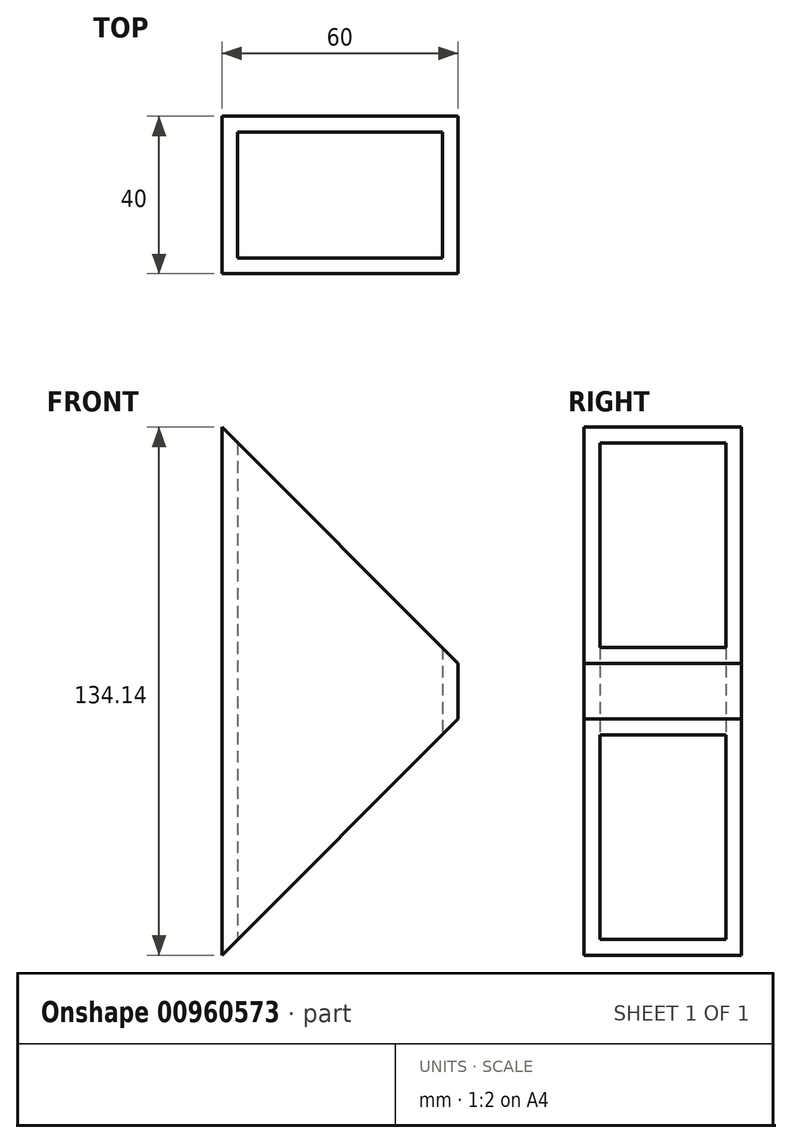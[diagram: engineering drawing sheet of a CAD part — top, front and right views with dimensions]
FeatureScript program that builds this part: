
annotation { "Feature Type Name" : "Feature", "Feature Type Description" : "" }
export const myFeature = defineFeature(function(context is Context, id is Id, definition is map)
    precondition{}
    {
        {
            var Q0;
            Q0=qCreatedBy(makeId("Top.planeOp"),FACE);
            var sketch = newSketch(context, id + "F0", { "sketchPlane" : qUnion([Q0])});
            skLineSegment(sketch, "E0.bottom", {"start": v(30, -20) * mm, "end": v(-30, -20) * mm});
            skLineSegment(sketch, "E0.top", {"start": v(30, 20) * mm, "end": v(-30, 20) * mm});
            skLineSegment(sketch, "E0.left", {"start": v(30, -20) * mm, "end": v(30, 20) * mm});
            skLineSegment(sketch, "E0.right", {"start": v(-30, -20) * mm, "end": v(-30, 20) * mm});
            skPoint(sketch, "E0.middle", {"position": v(0, 0) * mm});
            skLineSegment(sketch, "E1.bottom", {"start": v(26, -16) * mm, "end": v(-26, -16) * mm});
            skLineSegment(sketch, "E1.top", {"start": v(26, 16) * mm, "end": v(-26, 16) * mm});
            skLineSegment(sketch, "E1.left", {"start": v(26, -16) * mm, "end": v(26, 16) * mm});
            skLineSegment(sketch, "E1.right", {"start": v(-26, -16) * mm, "end": v(-26, 16) * mm});
            skSolve(sketch);
        }
        {
            var Q0;
            Q0 = qSketchRegion(id + "F0", true);
            extrude(context, id + "F1", {"entities" : qUnion([Q0]), "depth" : 170 * mm, "offsetDistance" : 25 * mm});
        }
        {
            var Q0;
            Q0=makeQuery(id+"F1.opExtrude","SWEPT_FACE",FACE,{"disambiguationData":[OSD([sQuery(id+"F0.wireOp",EDGE,"E0.bottom")])]});
            var sketch = newSketch(context, id + "F2", { "sketchPlane" : qUnion([Q0])});
            skLineSegment(sketch, "E2", {"start": v(-30, 0) * mm, "end": v(30, 60) * mm});
            skLineSegment(sketch, "E3", {"start": v(30, 60) * mm, "end": v(22.93, 67.07) * mm});
            skLineSegment(sketch, "E4", {"start": v(22.93, 67.07) * mm, "end": v(30, 74.14) * mm});
            skLineSegment(sketch, "E5", {"start": v(30, 74.14) * mm, "end": v(-30, 134.14) * mm});
            skLineSegment(sketch, "E6", {"start": v(-30, 134.14) * mm, "end": v(-30, 170) * mm});
            skLineSegment(sketch, "E7", {"start": v(-30, 170) * mm, "end": v(30, 170) * mm});
            skLineSegment(sketch, "E8", {"start": v(30, 170) * mm, "end": v(30, 74.14) * mm});
            skLineSegment(sketch, "E9", {"start": v(30, 60) * mm, "end": v(30, 0) * mm});
            skLineSegment(sketch, "E10", {"start": v(30, 0) * mm, "end": v(-30, 0) * mm});
            skSolve(sketch);
        }
        {
            var Q0;
            Q0 = qSketchRegion(id + "F2", true);
            extrude(context, id + "F3", {"entities" : qUnion([Q0]), "operationType" : NewBodyOperationType.REMOVE, "oppositeDirection" : true, "depth" : 40 * mm, "offsetDistance" : 25 * mm});
        }
    });
